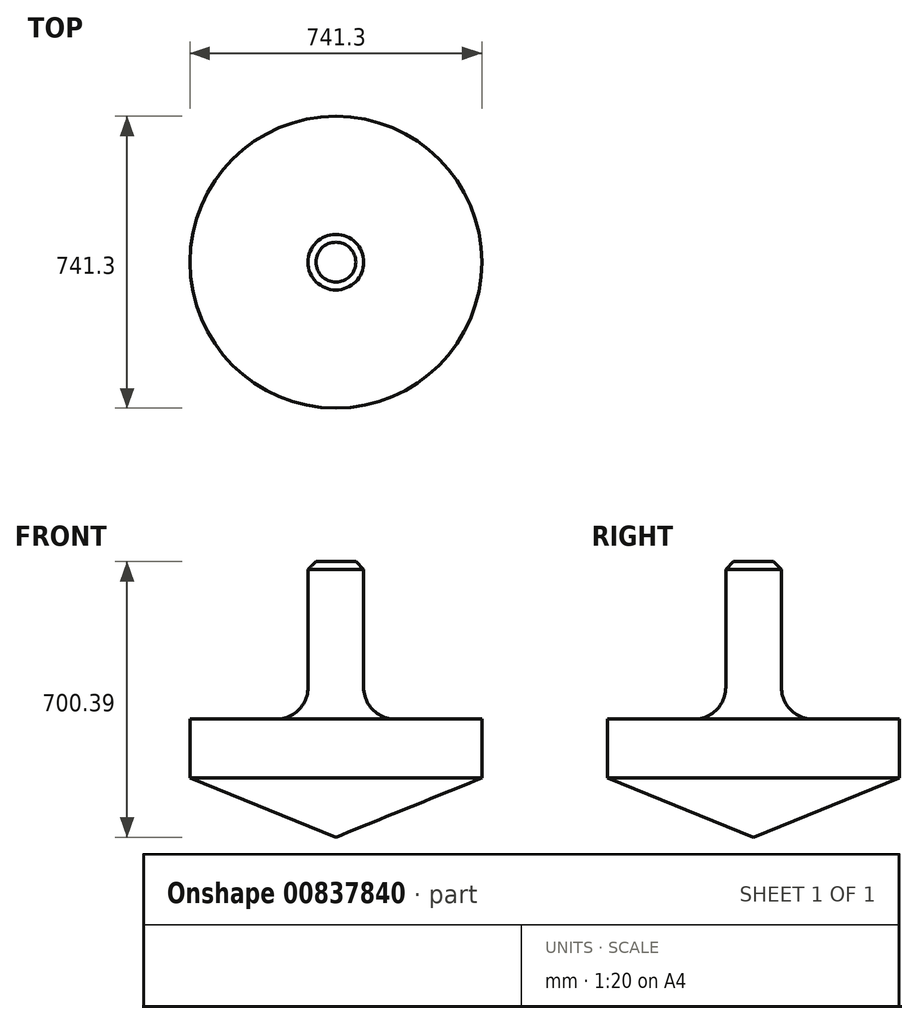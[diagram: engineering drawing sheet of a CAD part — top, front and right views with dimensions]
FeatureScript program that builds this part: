
annotation { "Feature Type Name" : "Feature", "Feature Type Description" : "" }
export const myFeature = defineFeature(function(context is Context, id is Id, definition is map)
    precondition{}
    {
        {
            var Q0;
            Q0=qCreatedBy(makeId("Front.planeOp"),FACE);
            var sketch = newSketch(context, id + "F0", { "sketchPlane" : qUnion([Q0])});
            skLineSegment(sketch, "E0", {"start": v(0, 350) * mm, "end": v(0, -350) * mm, "construction": true});
            skLineSegment(sketch, "E1", {"start": v(0, -350) * mm, "end": v(370.65, -199.61) * mm});
            skLineSegment(sketch, "E2", {"start": v(370.65, -199.61) * mm, "end": v(370.65, -49.61) * mm});
            skLineSegment(sketch, "E3", {"start": v(370.65, -49.61) * mm, "end": v(150.65, -49.61) * mm});
            skLineSegment(sketch, "E4", {"start": v(70.65, 30.39) * mm, "end": v(70.65, 350.39) * mm});
            skLineSegment(sketch, "E5", {"start": v(0, 350.39) * mm, "end": v(0, -350) * mm});
            skPoint(sketch, "E6.visualSharp", {"position": v(70.65, -49.61) * mm});
            skArc(sketch, "E6.filletArc", {"start": v(70.65, 30.39) * mm, "mid": v(94.08, -26.18) * mm, "end": v(150.65, -49.61) * mm});
            skLineSegment(sketch, "E7", {"start": v(70.65, 350.39) * mm, "end": v(0, 350.39) * mm});
            skSolve(sketch);
        }
        {
            var Q0;
            Q0 = qSketchRegion(id + "F0", true);
            var Q1;
            Q1=sQuery(id+"F0.wireOp",EDGE,"E5");
            revolve(context, id + "F1", {"surfaceOperationType" : NewSurfaceOperationType.NEW, "entities" : qUnion([Q0]), "axis" : qUnion([Q1]), "revolveType" : RevolveType.FULL});
        }
        {
            var Q0;
            Q0=makeQuery(id+"F1.opRevolve","SWEPT_EDGE",EDGE,{"disambiguationData":[OSD([sQuery(id+"F0.wireOp",EDGE,"E4"),sQuery(id+"F0.wireOp",EDGE,"1qzaCjyL-NMVr-zDQ1-omNt-5C6fuuugCwIs")])]});
            chamfer(context, id + "F2", {"entities" : qUnion([Q0]), "width" : 20 * mm, "tangentPropagation" : true});
        }
    });
